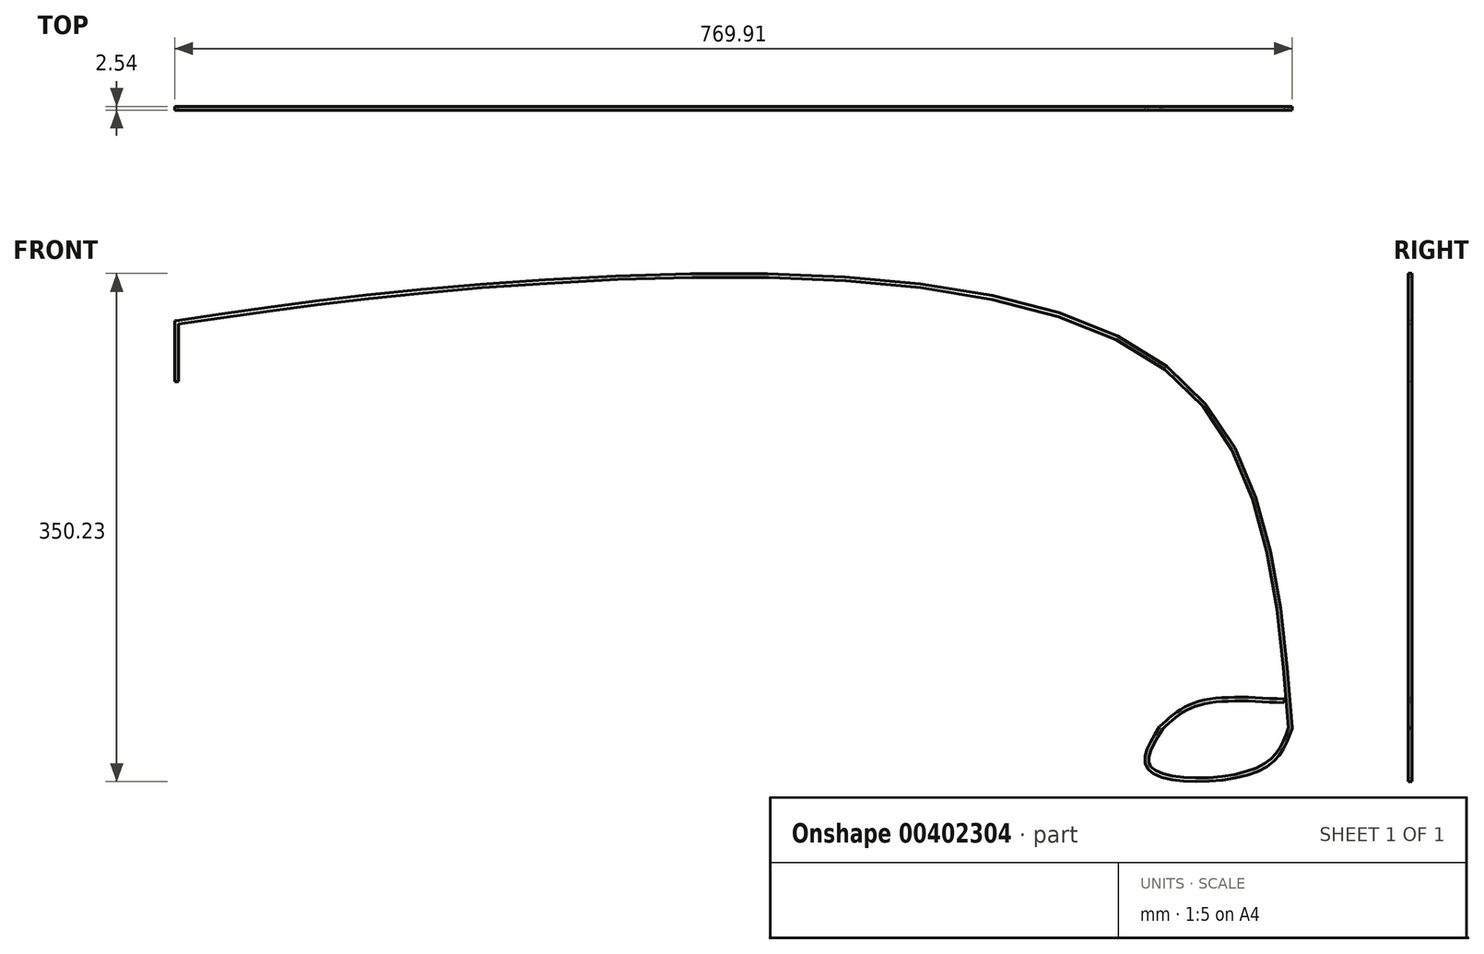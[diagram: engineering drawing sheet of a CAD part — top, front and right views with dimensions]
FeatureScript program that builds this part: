
annotation { "Feature Type Name" : "Feature", "Feature Type Description" : "" }
export const myFeature = defineFeature(function(context is Context, id is Id, definition is map)
    precondition{}
    {
        {
            var Q0;
            Q0=qCreatedBy(makeId("Top.planeOp"),FACE);
            var sketch = newSketch(context, id + "F0", { "sketchPlane" : qUnion([Q0])});
            skLineSegment(sketch, "E0.bottom", {"start": v(-1.27, 1.27) * mm, "end": v(1.27, 1.27) * mm});
            skLineSegment(sketch, "E0.top", {"start": v(-1.27, -1.27) * mm, "end": v(1.27, -1.27) * mm});
            skLineSegment(sketch, "E0.left", {"start": v(-1.27, 1.27) * mm, "end": v(-1.27, -1.27) * mm});
            skLineSegment(sketch, "E0.right", {"start": v(1.27, 1.27) * mm, "end": v(1.27, -1.27) * mm});
            skPoint(sketch, "E0.middle", {"position": v(0, 0) * mm});
            skSolve(sketch);
        }
        {
            var Q0;
            Q0=qCreatedBy(makeId("Front.planeOp"),FACE);
            var sketch = newSketch(context, id + "F1", { "sketchPlane" : qUnion([Q0])});
            skLineSegment(sketch, "E1", {"start": v(0, 0) * mm, "end": v(0, 40.64) * mm});
            skFitSpline(sketch, "E2", {"points": [v(0, 40.64) * mm, v(247.43, 68.45) * mm, v(679.42, 11.1) * mm, v(767.35, -238.66) * mm], "startDerivative": vector(714.65, 105.28) * mm, "endDerivative": vector(75.34, -955) * mm});
            skFitSpline(sketch, "E3", {"points": [v(767.35, -238.66) * mm, v(745.24, -267.18) * mm, v(670.88, -266.88) * mm, v(678.44, -238.66) * mm], "startDerivative": vector(-37.45, -109.54) * mm, "endDerivative": vector(76.77, 120.64) * mm});
            skFitSpline(sketch, "E4", {"points": [v(678.44, -238.66) * mm, v(702.68, -222.3) * mm, v(763.05, -220.27) * mm], "startDerivative": vector(50.2, 47.34) * mm, "endDerivative": vector(115.14, -7.3) * mm});
            skSolve(sketch);
        }
        {
            var Q0;
            Q0 = qSketchRegion(id + "F0", true);
            var Q1;
            Q1 = qConstructionFilter(qBodyType(qCreatedBy(id + "F1" ,EDGE), BodyType.WIRE), ConstructionObject.NO);
            sweep(context, id + "F2", {"profiles" : qUnion([Q0]), "path" : qUnion([Q1])});
        }
    });
